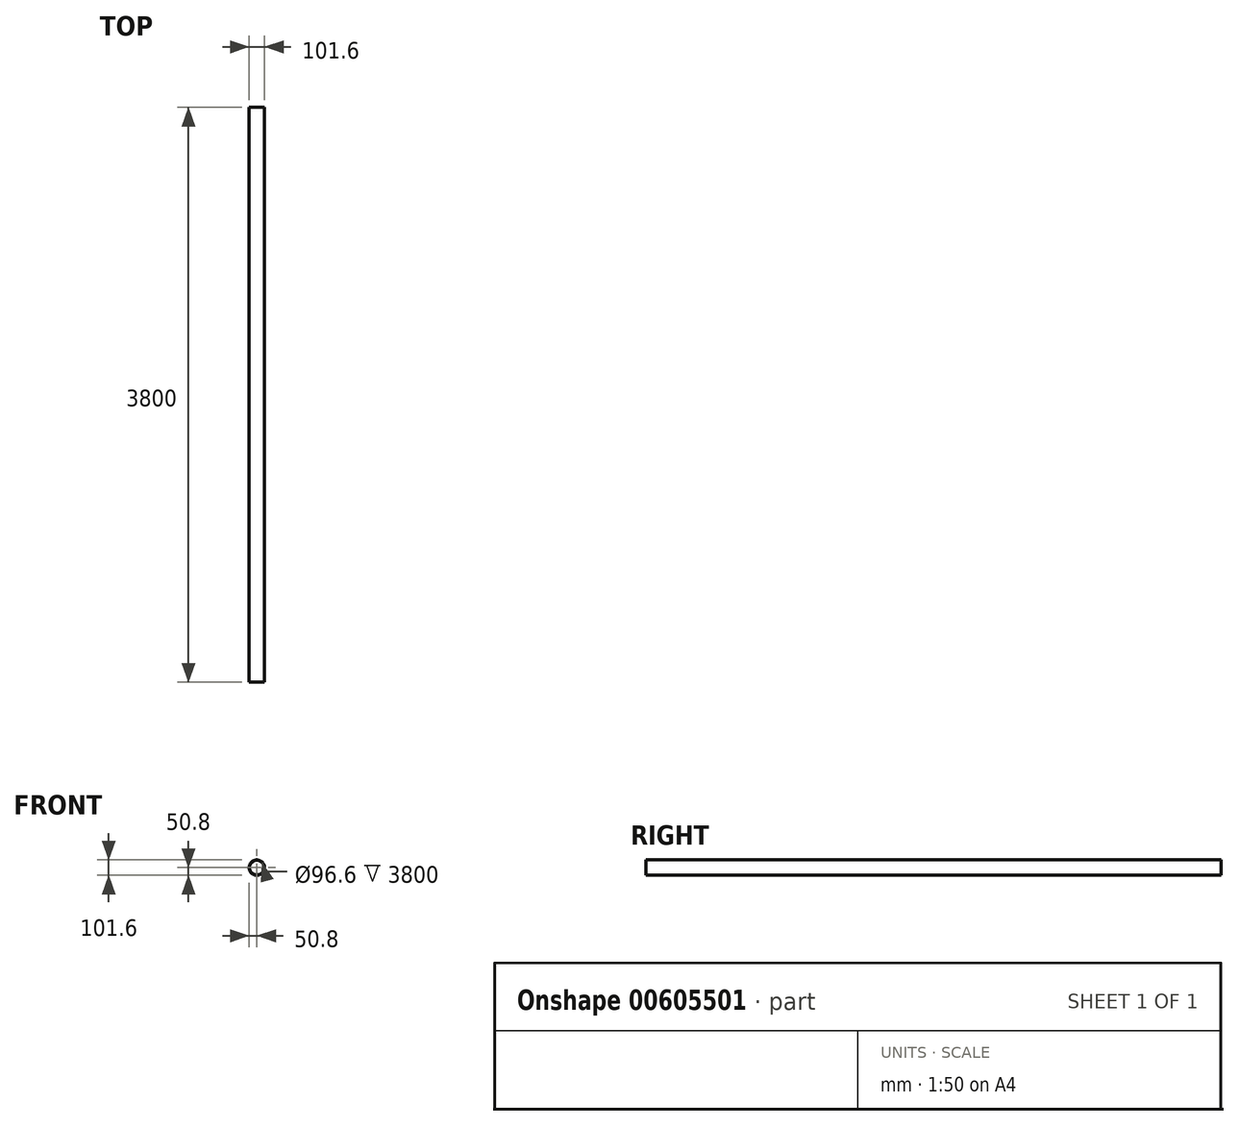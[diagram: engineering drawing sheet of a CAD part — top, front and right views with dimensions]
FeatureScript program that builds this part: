
annotation { "Feature Type Name" : "Feature", "Feature Type Description" : "" }
export const myFeature = defineFeature(function(context is Context, id is Id, definition is map)
    precondition{}
    {
        {
            var Q0;
            Q0=qCreatedBy(makeId("Front.planeOp"),FACE);
            var sketch = newSketch(context, id + "F0", { "sketchPlane" : qUnion([Q0])});
            skCircle(sketch, "E0", {"center": v(0, 0) * mm, "radius": 50.8 * mm});
            skCircle(sketch, "E1.0", {"center": v(0, 0) * mm, "radius": 48.3 * mm});
            skSolve(sketch);
        }
        {
            var Q0;
            Q0 = qSketchRegion(id + "F0", true);
            extrude(context, id + "F1", {"entities" : qUnion([Q0]), "depth" : 3800 * mm, "offsetDistance" : 25 * mm});
        }
    });
